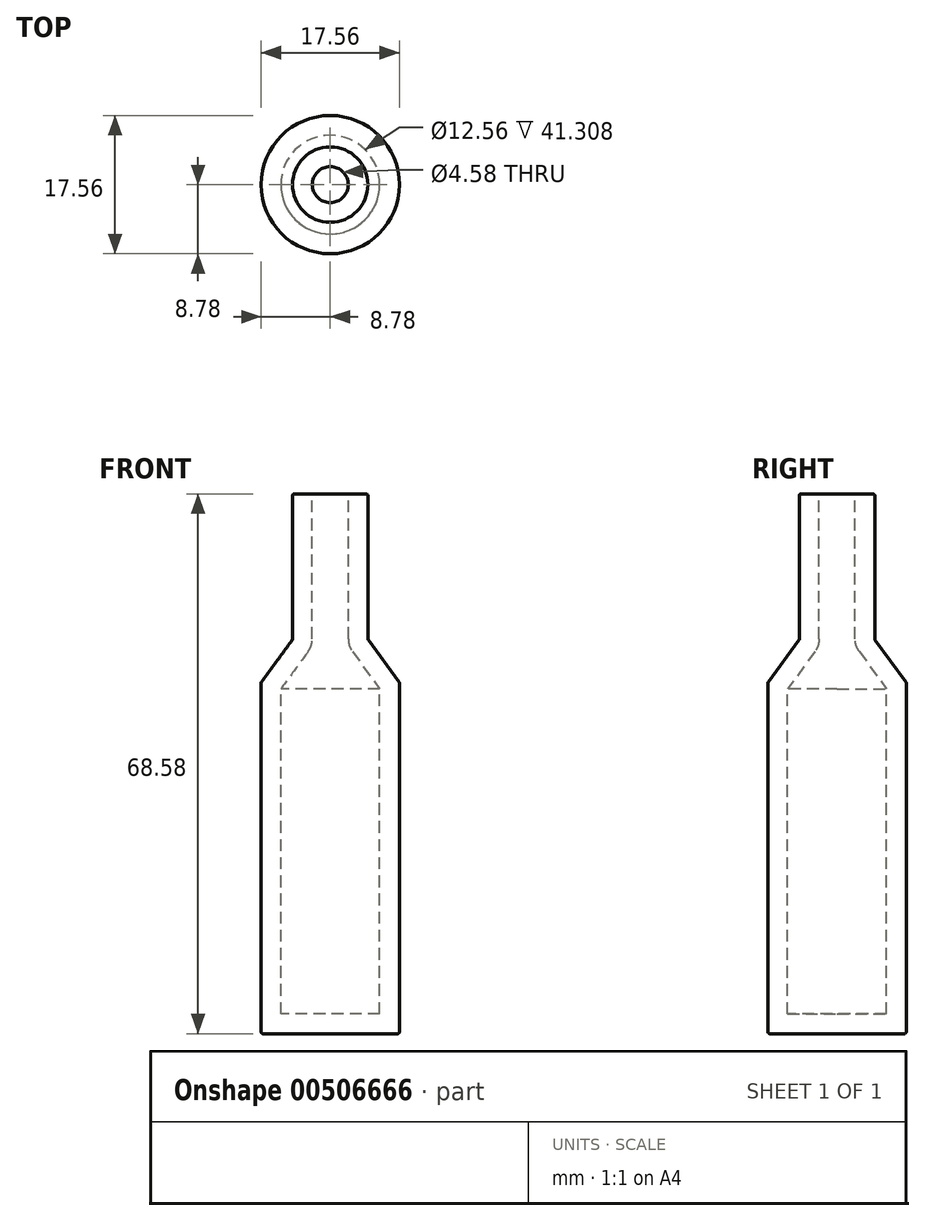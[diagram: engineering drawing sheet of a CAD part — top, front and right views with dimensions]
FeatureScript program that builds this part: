
annotation { "Feature Type Name" : "Feature", "Feature Type Description" : "" }
export const myFeature = defineFeature(function(context is Context, id is Id, definition is map)
    precondition{}
    {
        {
            var Q0;
            Q0=qCreatedBy(makeId("Front.planeOp"),FACE);
            var sketch = newSketch(context, id + "F0", { "sketchPlane" : qUnion([Q0])});
            skLineSegment(sketch, "E0", {"start": v(0, 0) * mm, "end": v(8.78, 0) * mm});
            skLineSegment(sketch, "E1", {"start": v(8.78, 0) * mm, "end": v(8.78, 44.63) * mm});
            skLineSegment(sketch, "E2", {"start": v(8.78, 44.63) * mm, "end": v(4.79, 50.07) * mm});
            skLineSegment(sketch, "E3", {"start": v(4.79, 50.07) * mm, "end": v(4.79, 68.58) * mm});
            skLineSegment(sketch, "E4", {"start": v(4.79, 68.58) * mm, "end": v(0, 68.58) * mm});
            skLineSegment(sketch, "E5", {"start": v(0, 68.58) * mm, "end": v(0, 0) * mm});
            skSolve(sketch);
        }
        {
            var Q0;
            Q0 = qSketchRegion(id + "F0", true);
            var Q1;
            Q1=sQuery(id+"F0.wireOp",EDGE,"E5");
            revolve(context, id + "F1", {"entities" : qUnion([Q0]), "axis" : qUnion([Q1]), "revolveType" : RevolveType.FULL});
        }
        {
            var Q0;
            Q0=makeQuery(id+"F1.opRevolve","SWEPT_FACE",FACE,{"disambiguationData":[OSD([sQuery(id+"F0.wireOp",EDGE,"E2")])]});
            var Q1;
            Q1=makeQuery(id+"F1.opRevolve","SWEPT_EDGE",EDGE,{"disambiguationData":[OSD([sQuery(id+"F0.wireOp",EDGE,"E3"),sQuery(id+"F0.wireOp",EDGE,"E4")])]});
            var Q2;
            Q2=makeQuery(id+"F1.opRevolve","SWEPT_FACE",FACE,{"disambiguationData":[OSD([sQuery(id+"F0.wireOp",EDGE,"E3")])]});
            var Q3;
            Q3=makeQuery(id+"F1.opRevolve","SWEPT_FACE",FACE,{"disambiguationData":[OSD([sQuery(id+"F0.wireOp",EDGE,"E4")])]});
            var Q4;
            Q4=makeQuery(id+"F1.opRevolve","SWEPT_EDGE",EDGE,{"disambiguationData":[OSD([sQuery(id+"F0.wireOp",EDGE,"E0"),sQuery(id+"F0.wireOp",EDGE,"E1")])]});
            fillet(context, id + "F2", {"entities" : qUnion([Q0, Q1, Q2, Q3, Q4]), "radius" : 0.24 * mm, "tangentPropagation" : true, "allowEdgeOverflow" : false});
        }
        {
            var Q0;
            Q0=makeQuery(id+"F1.opRevolve","SWEPT_FACE",FACE,{"disambiguationData":[OSD([sQuery(id+"F0.wireOp",EDGE,"E4")])]});
            shell(context, id + "F3", {"entities" : qUnion([Q0]), "thickness" : 2.5 * mm});
        }
    });
